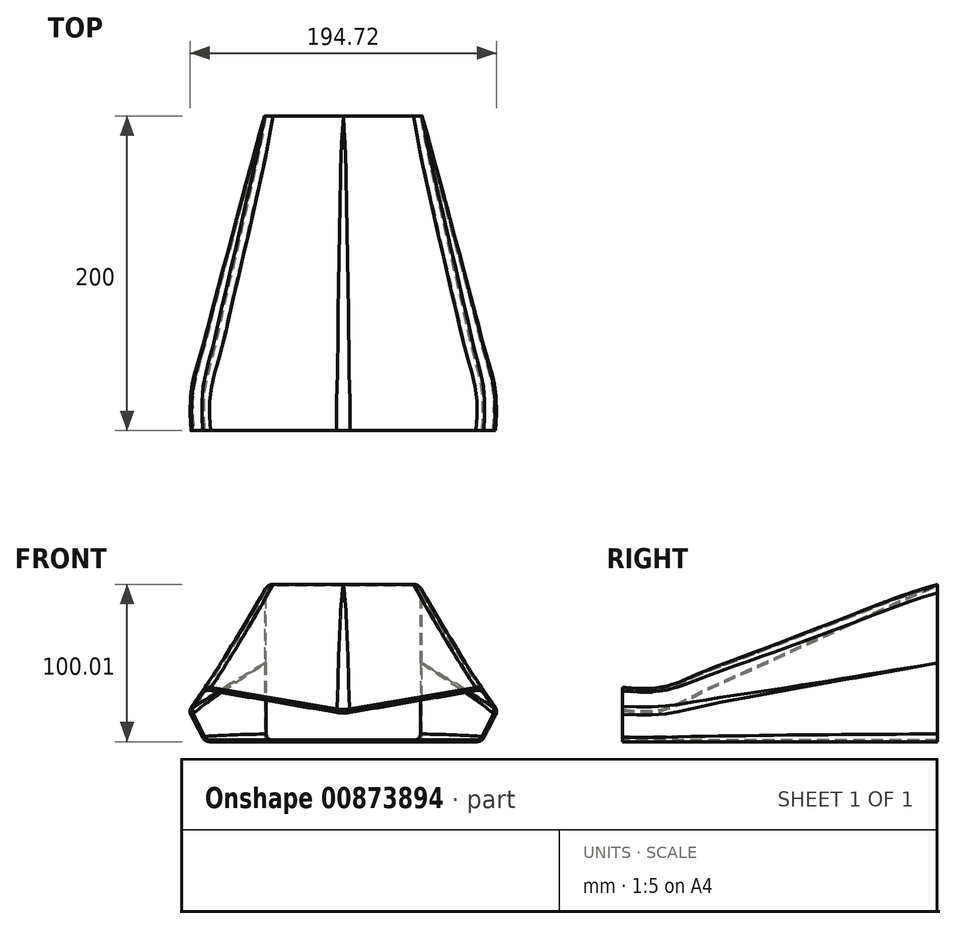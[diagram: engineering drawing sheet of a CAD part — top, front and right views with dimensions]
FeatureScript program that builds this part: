
annotation { "Feature Type Name" : "Feature", "Feature Type Description" : "" }
export const myFeature = defineFeature(function(context is Context, id is Id, definition is map)
    precondition{}
    {
        {
            var Q0;
            Q0=qCreatedBy(makeId("Front.planeOp"),FACE);
            var sketch = newSketch(context, id + "F0", { "sketchPlane" : qUnion([Q0])});
            skLineSegment(sketch, "E0.bottom", {"start": v(50, -50) * mm, "end": v(-50, -50) * mm});
            skLineSegment(sketch, "E0.top", {"start": v(50, 50) * mm, "end": v(-50, 50) * mm});
            skLineSegment(sketch, "E0.left", {"start": v(50, -50) * mm, "end": v(50, 50) * mm});
            skLineSegment(sketch, "E0.right", {"start": v(-50, -50) * mm, "end": v(-50, 50) * mm});
            skPoint(sketch, "E0.middle", {"position": v(0, 0) * mm});
            skPoint(sketch, "E1", {"position": v(-50, 0) * mm});
            skPoint(sketch, "E2", {"position": v(50, 0) * mm});
            skPoint(sketch, "E3", {"position": v(0, 50) * mm});
            skSolve(sketch);
        }
        {
            var Q0;
            Q0=qCreatedBy(makeId("Front.planeOp"),FACE);
            cPlane(context, id + "F1", {"entities" : qUnion([Q0]), "cplaneType" : CPlaneType.OFFSET, "offset" : 200 * mm, "width" : 150 * mm, "height" : 150 * mm});
        }
        {
            var Q0;
            Q0=qCreatedBy(id+"F1.planeOp",FACE);
            var sketch = newSketch(context, id + "F2", { "sketchPlane" : qUnion([Q0])});
            skLineSegment(sketch, "E4.0.0", {"start": v(50, -50) * mm, "end": v(50, 50) * mm, "construction": true});
            skLineSegment(sketch, "E4.0.1", {"start": v(50, 50) * mm, "end": v(-50, 50) * mm, "construction": true});
            skLineSegment(sketch, "E4.0.2", {"start": v(-50, 50) * mm, "end": v(-50, -50) * mm, "construction": true});
            skLineSegment(sketch, "E4.0.3", {"start": v(-50, -50) * mm, "end": v(50, -50) * mm, "construction": true});
            skLineSegment(sketch, "E5", {"start": v(-87.5, -50) * mm, "end": v(87.5, -50) * mm});
            skPoint(sketch, "E6", {"position": v(0, -50) * mm});
            skLineSegment(sketch, "E7", {"start": v(-87.5, -50) * mm, "end": v(-97.5, -30) * mm});
            skLineSegment(sketch, "E8", {"start": v(-97.5, -30) * mm, "end": v(-87.5, -15) * mm});
            skLineSegment(sketch, "E9", {"start": v(-87.5, -15) * mm, "end": v(0, -30) * mm});
            skLineSegment(sketch, "E10", {"start": v(0, -30) * mm, "end": v(87.5, -15) * mm});
            skLineSegment(sketch, "E11", {"start": v(87.5, -15) * mm, "end": v(97.5, -30) * mm});
            skLineSegment(sketch, "E12", {"start": v(97.5, -30) * mm, "end": v(87.5, -50) * mm});
            skLineSegment(sketch, "E13", {"start": v(-97.5, -30) * mm, "end": v(97.5, -30) * mm, "construction": true});
            skPoint(sketch, "E14", {"position": v(0, -30) * mm});
            skLineSegment(sketch, "E15", {"start": v(-87.5, -15) * mm, "end": v(87.5, -15) * mm, "construction": true});
            skPoint(sketch, "E16", {"position": v(0, -15) * mm});
            skSolve(sketch);
        }
        {
            var Q0;
            Q0=qCreatedBy(makeId("Front.planeOp"),FACE);
            cPlane(context, id + "F3", {"entities" : qUnion([Q0]), "cplaneType" : CPlaneType.OFFSET, "offset" : 175 * mm, "width" : 150 * mm, "height" : 150 * mm});
        }
        {
            var Q0;
            Q0=qCreatedBy(id+"F3.planeOp",FACE);
            var sketch = newSketch(context, id + "F4", { "sketchPlane" : qUnion([Q0])});
            skLineSegment(sketch, "E17.0.0", {"start": v(87.5, -50) * mm, "end": v(97.5, -30) * mm});
            skLineSegment(sketch, "E17.0.1", {"start": v(97.5, -30) * mm, "end": v(87.5, -15) * mm});
            skLineSegment(sketch, "E17.0.2", {"start": v(87.5, -15) * mm, "end": v(0, -30) * mm});
            skLineSegment(sketch, "E17.0.3", {"start": v(0, -30) * mm, "end": v(-87.5, -15) * mm});
            skLineSegment(sketch, "E17.0.4", {"start": v(-87.5, -15) * mm, "end": v(-97.5, -30) * mm});
            skLineSegment(sketch, "E17.0.5", {"start": v(-97.5, -30) * mm, "end": v(-87.5, -50) * mm});
            skLineSegment(sketch, "E17.0.6", {"start": v(-87.5, -50) * mm, "end": v(87.5, -50) * mm});
            skSolve(sketch);
        }
        {
            var Q0;
            Q0=qCreatedBy(makeId("Front.planeOp"),FACE);
            cPlane(context, id + "F5", {"entities" : qUnion([Q0]), "cplaneType" : CPlaneType.OFFSET, "offset" : 150 * mm, "width" : 150 * mm, "height" : 150 * mm});
        }
        {
            var Q0;
            Q0=qCreatedBy(id+"F5.planeOp",FACE);
            var sketch = newSketch(context, id + "F6", { "sketchPlane" : qUnion([Q0])});
            skPoint(sketch, "E18.0", {"position": v(-50, 50) * mm});
            skPoint(sketch, "E19.0", {"position": v(50, 50) * mm});
            skPoint(sketch, "E20.0", {"position": v(0, 50) * mm});
            skPoint(sketch, "E21.0", {"position": v(50, 0) * mm});
            skPoint(sketch, "E22.0", {"position": v(50, -50) * mm});
            skPoint(sketch, "E23.0", {"position": v(-50, 0) * mm});
            skPoint(sketch, "E24.0", {"position": v(-50, -50) * mm});
            skPoint(sketch, "E25.0", {"position": v(-87.5, -50) * mm});
            skPoint(sketch, "E26.0", {"position": v(-97.5, -30) * mm});
            skPoint(sketch, "E27.0", {"position": v(-87.5, -15) * mm});
            skPoint(sketch, "E28.0", {"position": v(87.5, -50) * mm});
            skPoint(sketch, "E29.0", {"position": v(97.5, -30) * mm});
            skPoint(sketch, "E30.0", {"position": v(87.5, -15) * mm});
            skLineSegment(sketch, "E31", {"start": v(-87.5, -15) * mm, "end": v(-50, 50) * mm, "construction": true});
            skLineSegment(sketch, "E32", {"start": v(-97.5, -30) * mm, "end": v(-50, 0) * mm, "construction": true});
            skLineSegment(sketch, "E33", {"start": v(-87.5, -50) * mm, "end": v(-50, -50) * mm, "construction": true});
            skPoint(sketch, "E34.0", {"position": v(0, -30) * mm});
            skLineSegment(sketch, "E35", {"start": v(0, -30) * mm, "end": v(0, 50) * mm, "construction": true});
            skLineSegment(sketch, "E36", {"start": v(87.5, -15) * mm, "end": v(50, 50) * mm, "construction": true});
            skLineSegment(sketch, "E37", {"start": v(97.5, -30) * mm, "end": v(50, 0) * mm, "construction": true});
            skLineSegment(sketch, "E38", {"start": v(87.5, -50) * mm, "end": v(50, -50) * mm, "construction": true});
            skPoint(sketch, "E39", {"position": v(-82, -50) * mm});
            skPoint(sketch, "E40", {"position": v(82, -50) * mm});
            skPoint(sketch, "E41", {"position": v(-90.74, -25.73) * mm});
            skPoint(sketch, "E42", {"position": v(90.74, -25.73) * mm});
            skPoint(sketch, "E43", {"position": v(-82, -5.47) * mm});
            skPoint(sketch, "E44", {"position": v(82, -5.47) * mm});
            skPoint(sketch, "E45", {"position": v(0, -18.5) * mm});
            skLineSegment(sketch, "E46", {"start": v(-82, -50) * mm, "end": v(82, -50) * mm});
            skLineSegment(sketch, "E47", {"start": v(82, -50) * mm, "end": v(90.74, -25.73) * mm});
            skLineSegment(sketch, "E48", {"start": v(90.74, -25.73) * mm, "end": v(82, -5.47) * mm});
            skLineSegment(sketch, "E49", {"start": v(82, -5.47) * mm, "end": v(0, -18.5) * mm});
            skLineSegment(sketch, "E50", {"start": v(0, -18.5) * mm, "end": v(-82, -5.47) * mm});
            skLineSegment(sketch, "E51", {"start": v(-82, -5.47) * mm, "end": v(-90.74, -25.73) * mm});
            skLineSegment(sketch, "E52", {"start": v(-90.74, -25.73) * mm, "end": v(-82, -50) * mm});
            skSolve(sketch);
        }
        {
            var Q0;
            Q0=qCreatedBy(makeId("Front.planeOp"),FACE);
            cPlane(context, id + "F7", {"entities" : qUnion([Q0]), "cplaneType" : CPlaneType.OFFSET, "offset" : 125 * mm, "width" : 150 * mm, "height" : 150 * mm});
        }
        {
            var Q0;
            Q0=qCreatedBy(id+"F7.planeOp",FACE);
            var sketch = newSketch(context, id + "F8", { "sketchPlane" : qUnion([Q0])});
            skPoint(sketch, "E53.0", {"position": v(-82, -50) * mm});
            skPoint(sketch, "E54.0", {"position": v(-90.74, -25.73) * mm});
            skPoint(sketch, "E55.0", {"position": v(-82, -5.47) * mm});
            skPoint(sketch, "E56.0", {"position": v(0, -18.5) * mm});
            skPoint(sketch, "E57.0", {"position": v(82, -5.47) * mm});
            skPoint(sketch, "E58.0", {"position": v(90.74, -25.73) * mm});
            skPoint(sketch, "E59.0", {"position": v(82, -50) * mm});
            skLineSegment(sketch, "E60.0", {"start": v(-87.5, -50) * mm, "end": v(-50, -50) * mm, "construction": true});
            skLineSegment(sketch, "E61.0", {"start": v(-97.5, -30) * mm, "end": v(-50, 0) * mm, "construction": true});
            skLineSegment(sketch, "E62.0", {"start": v(-87.5, -15) * mm, "end": v(-50, 50) * mm, "construction": true});
            skLineSegment(sketch, "E63.0", {"start": v(0, -30) * mm, "end": v(0, 50) * mm, "construction": true});
            skLineSegment(sketch, "E64.0", {"start": v(87.5, -15) * mm, "end": v(50, 50) * mm, "construction": true});
            skLineSegment(sketch, "E65.0", {"start": v(97.5, -30) * mm, "end": v(50, 0) * mm, "construction": true});
            skLineSegment(sketch, "E66.0", {"start": v(87.5, -50) * mm, "end": v(50, -50) * mm, "construction": true});
            skPoint(sketch, "E67", {"position": v(-76.5, -50) * mm});
            skPoint(sketch, "E68", {"position": v(-83.97, -21.46) * mm});
            skPoint(sketch, "E69", {"position": v(-76.5, 4.06) * mm});
            skPoint(sketch, "E70", {"position": v(76.5, 4.06) * mm});
            skPoint(sketch, "E71", {"position": v(83.97, -21.46) * mm});
            skPoint(sketch, "E72", {"position": v(76.5, -50) * mm});
            skPoint(sketch, "E73", {"position": v(0, -7) * mm});
            skLineSegment(sketch, "E74", {"start": v(-76.5, -50) * mm, "end": v(76.5, -50) * mm});
            skLineSegment(sketch, "E75", {"start": v(76.5, -50) * mm, "end": v(83.97, -21.46) * mm});
            skLineSegment(sketch, "E76", {"start": v(83.97, -21.46) * mm, "end": v(76.5, 4.06) * mm});
            skLineSegment(sketch, "E77", {"start": v(76.5, 4.06) * mm, "end": v(0, -7) * mm});
            skLineSegment(sketch, "E78", {"start": v(0, -7) * mm, "end": v(-76.5, 4.06) * mm});
            skLineSegment(sketch, "E79", {"start": v(-76.5, 4.06) * mm, "end": v(-83.97, -21.46) * mm});
            skLineSegment(sketch, "E80", {"start": v(-83.97, -21.46) * mm, "end": v(-76.5, -50) * mm});
            skSolve(sketch);
        }
        {
            var Q0;
            Q0=qCreatedBy(makeId("Front.planeOp"),FACE);
            cPlane(context, id + "F9", {"entities" : qUnion([Q0]), "cplaneType" : CPlaneType.OFFSET, "offset" : 100 * mm, "width" : 150 * mm, "height" : 150 * mm});
        }
        {
            var Q0;
            Q0=qCreatedBy(id+"F9.planeOp",FACE);
            var sketch = newSketch(context, id + "F10", { "sketchPlane" : qUnion([Q0])});
            skPoint(sketch, "E81.0", {"position": v(-76.5, -50) * mm});
            skPoint(sketch, "E82.0", {"position": v(-83.97, -21.46) * mm});
            skPoint(sketch, "E83.0", {"position": v(-76.5, 4.06) * mm});
            skPoint(sketch, "E84.0", {"position": v(0, -7) * mm});
            skPoint(sketch, "E85.0", {"position": v(76.5, 4.06) * mm});
            skPoint(sketch, "E86.0", {"position": v(83.97, -21.46) * mm});
            skPoint(sketch, "E87.0", {"position": v(76.5, -50) * mm});
            skLineSegment(sketch, "E88.0", {"start": v(-87.5, -50) * mm, "end": v(-50, -50) * mm, "construction": true});
            skLineSegment(sketch, "E89.0", {"start": v(-97.5, -30) * mm, "end": v(-50, 0) * mm, "construction": true});
            skLineSegment(sketch, "E90.0", {"start": v(-87.5, -15) * mm, "end": v(-50, 50) * mm, "construction": true});
            skLineSegment(sketch, "E91.0", {"start": v(0, -30) * mm, "end": v(0, 50) * mm, "construction": true});
            skLineSegment(sketch, "E92.0", {"start": v(87.5, -15) * mm, "end": v(50, 50) * mm, "construction": true});
            skLineSegment(sketch, "E93.0", {"start": v(97.5, -30) * mm, "end": v(50, 0) * mm, "construction": true});
            skLineSegment(sketch, "E94.0", {"start": v(87.5, -50) * mm, "end": v(50, -50) * mm, "construction": true});
            skPoint(sketch, "E95", {"position": v(-71, -50) * mm});
            skPoint(sketch, "E96", {"position": v(71, -50) * mm});
            skPoint(sketch, "E97", {"position": v(77.2, -17.18) * mm});
            skPoint(sketch, "E98", {"position": v(-77.2, -17.18) * mm});
            skPoint(sketch, "E99", {"position": v(-71, 13.58) * mm});
            skPoint(sketch, "E100", {"position": v(71, 13.58) * mm});
            skPoint(sketch, "E101", {"position": v(0, 4.5) * mm});
            skLineSegment(sketch, "E102", {"start": v(71, -50) * mm, "end": v(-71, -50) * mm});
            skLineSegment(sketch, "E103", {"start": v(-71, -50) * mm, "end": v(-77.2, -17.18) * mm});
            skLineSegment(sketch, "E104", {"start": v(-77.2, -17.18) * mm, "end": v(-71, 13.58) * mm});
            skLineSegment(sketch, "E105", {"start": v(-71, 13.58) * mm, "end": v(0, 4.5) * mm});
            skLineSegment(sketch, "E106", {"start": v(0, 4.5) * mm, "end": v(71, 13.58) * mm});
            skLineSegment(sketch, "E107", {"start": v(71, 13.58) * mm, "end": v(77.2, -17.18) * mm});
            skLineSegment(sketch, "E108", {"start": v(77.2, -17.18) * mm, "end": v(71, -50) * mm});
            skSolve(sketch);
        }
        {
            var Q0;
            Q0=qCreatedBy(makeId("Front.planeOp"),FACE);
            cPlane(context, id + "F11", {"entities" : qUnion([Q0]), "cplaneType" : CPlaneType.OFFSET, "offset" : 75 * mm, "width" : 150 * mm, "height" : 150 * mm});
        }
        {
            var Q0;
            Q0=qCreatedBy(id+"F11.planeOp",FACE);
            var sketch = newSketch(context, id + "F12", { "sketchPlane" : qUnion([Q0])});
            skPoint(sketch, "E109.0", {"position": v(-71, -50) * mm});
            skPoint(sketch, "E110.0", {"position": v(-77.2, -17.18) * mm});
            skPoint(sketch, "E111.0", {"position": v(-71, 13.58) * mm});
            skPoint(sketch, "E112.0", {"position": v(0, 4.5) * mm});
            skPoint(sketch, "E113.0", {"position": v(71, 13.58) * mm});
            skPoint(sketch, "E114.0", {"position": v(77.2, -17.18) * mm});
            skPoint(sketch, "E115.0", {"position": v(71, -50) * mm});
            skLineSegment(sketch, "E116.0", {"start": v(-87.5, -50) * mm, "end": v(-50, -50) * mm, "construction": true});
            skLineSegment(sketch, "E117.0", {"start": v(-97.5, -30) * mm, "end": v(-50, 0) * mm, "construction": true});
            skLineSegment(sketch, "E118.0", {"start": v(-87.5, -15) * mm, "end": v(-50, 50) * mm, "construction": true});
            skLineSegment(sketch, "E119.0", {"start": v(0, -30) * mm, "end": v(0, 50) * mm, "construction": true});
            skLineSegment(sketch, "E120.0", {"start": v(87.5, -15) * mm, "end": v(50, 50) * mm, "construction": true});
            skLineSegment(sketch, "E121.0", {"start": v(97.5, -30) * mm, "end": v(50, 0) * mm, "construction": true});
            skLineSegment(sketch, "E122.0", {"start": v(87.5, -50) * mm, "end": v(50, -50) * mm, "construction": true});
            skPoint(sketch, "E123", {"position": v(-65.5, -50) * mm});
            skPoint(sketch, "E124", {"position": v(65.5, -50) * mm});
            skPoint(sketch, "E125", {"position": v(70.44, -12.91) * mm});
            skPoint(sketch, "E126", {"position": v(-70.44, -12.91) * mm});
            skPoint(sketch, "E127", {"position": v(-65.51, 23.11) * mm});
            skPoint(sketch, "E128", {"position": v(65.51, 23.11) * mm});
            skPoint(sketch, "E129", {"position": v(0, 16) * mm});
            skLineSegment(sketch, "E130", {"start": v(-65.5, -50) * mm, "end": v(65.5, -50) * mm});
            skLineSegment(sketch, "E131", {"start": v(65.5, -50) * mm, "end": v(70.44, -12.91) * mm});
            skLineSegment(sketch, "E132", {"start": v(70.44, -12.91) * mm, "end": v(65.51, 23.11) * mm});
            skLineSegment(sketch, "E133", {"start": v(65.51, 23.11) * mm, "end": v(0, 16) * mm});
            skLineSegment(sketch, "E134", {"start": v(0, 16) * mm, "end": v(-65.51, 23.11) * mm});
            skLineSegment(sketch, "E135", {"start": v(-65.51, 23.11) * mm, "end": v(-70.44, -12.91) * mm});
            skLineSegment(sketch, "E136", {"start": v(-70.44, -12.91) * mm, "end": v(-65.5, -50) * mm});
            skSolve(sketch);
        }
        {
            var Q0;
            Q0=qCreatedBy(makeId("Front.planeOp"),FACE);
            cPlane(context, id + "F13", {"entities" : qUnion([Q0]), "cplaneType" : CPlaneType.OFFSET, "offset" : 50 * mm, "width" : 150 * mm, "height" : 150 * mm});
        }
        {
            var Q0;
            Q0=qCreatedBy(id+"F13.planeOp",FACE);
            var sketch = newSketch(context, id + "F14", { "sketchPlane" : qUnion([Q0])});
            skPoint(sketch, "E137.0", {"position": v(-65.5, -50) * mm});
            skPoint(sketch, "E138.0", {"position": v(-70.44, -12.91) * mm});
            skPoint(sketch, "E139.0", {"position": v(-65.51, 23.11) * mm});
            skPoint(sketch, "E140.0", {"position": v(0, 16) * mm});
            skPoint(sketch, "E141.0", {"position": v(65.51, 23.11) * mm});
            skPoint(sketch, "E142.0", {"position": v(70.44, -12.91) * mm});
            skPoint(sketch, "E143.0", {"position": v(65.5, -50) * mm});
            skLineSegment(sketch, "E144.0", {"start": v(-87.5, -50) * mm, "end": v(-50, -50) * mm, "construction": true});
            skLineSegment(sketch, "E145.0", {"start": v(-97.5, -30) * mm, "end": v(-50, 0) * mm, "construction": true});
            skLineSegment(sketch, "E146.0", {"start": v(-87.5, -15) * mm, "end": v(-50, 50) * mm, "construction": true});
            skLineSegment(sketch, "E147.0", {"start": v(87.5, -15) * mm, "end": v(50, 50) * mm, "construction": true});
            skLineSegment(sketch, "E148.0", {"start": v(97.5, -30) * mm, "end": v(50, 0) * mm, "construction": true});
            skLineSegment(sketch, "E149.0", {"start": v(87.5, -50) * mm, "end": v(50, -50) * mm, "construction": true});
            skLineSegment(sketch, "E150.0", {"start": v(0, -30) * mm, "end": v(0, 50) * mm, "construction": true});
            skPoint(sketch, "E151", {"position": v(-60, -50) * mm});
            skPoint(sketch, "E152", {"position": v(60, -50) * mm});
            skPoint(sketch, "E153", {"position": v(63.68, -8.64) * mm});
            skPoint(sketch, "E154", {"position": v(-63.68, -8.64) * mm});
            skPoint(sketch, "E155", {"position": v(-60.02, 32.64) * mm});
            skPoint(sketch, "E156", {"position": v(60.02, 32.64) * mm});
            skPoint(sketch, "E157", {"position": v(0, 27.5) * mm});
            skLineSegment(sketch, "E158", {"start": v(-60, -50) * mm, "end": v(60, -50) * mm});
            skLineSegment(sketch, "E159", {"start": v(60, -50) * mm, "end": v(63.68, -8.64) * mm});
            skLineSegment(sketch, "E160", {"start": v(63.68, -8.64) * mm, "end": v(60.02, 32.64) * mm});
            skLineSegment(sketch, "E161", {"start": v(60.02, 32.64) * mm, "end": v(0, 27.5) * mm});
            skLineSegment(sketch, "E162", {"start": v(0, 27.5) * mm, "end": v(-60.02, 32.64) * mm});
            skLineSegment(sketch, "E163", {"start": v(-60.02, 32.64) * mm, "end": v(-63.68, -8.64) * mm});
            skLineSegment(sketch, "E164", {"start": v(-63.68, -8.64) * mm, "end": v(-60, -50) * mm});
            skSolve(sketch);
        }
        {
            var Q0;
            Q0=qCreatedBy(makeId("Front.planeOp"),FACE);
            cPlane(context, id + "F15", {"entities" : qUnion([Q0]), "cplaneType" : CPlaneType.OFFSET, "offset" : 25 * mm, "width" : 150 * mm, "height" : 150 * mm});
        }
        {
            var Q0;
            Q0=qCreatedBy(id+"F15.planeOp",FACE);
            var sketch = newSketch(context, id + "F16", { "sketchPlane" : qUnion([Q0])});
            skPoint(sketch, "E165.0", {"position": v(-60, -50) * mm});
            skPoint(sketch, "E166.0", {"position": v(-63.68, -8.64) * mm});
            skPoint(sketch, "E167.0", {"position": v(-60.02, 32.64) * mm});
            skPoint(sketch, "E168.0", {"position": v(0, 27.5) * mm});
            skPoint(sketch, "E169.0", {"position": v(60.02, 32.64) * mm});
            skPoint(sketch, "E170.0", {"position": v(63.68, -8.64) * mm});
            skPoint(sketch, "E171.0", {"position": v(60, -50) * mm});
            skLineSegment(sketch, "E172.0", {"start": v(-87.5, -50) * mm, "end": v(-50, -50) * mm, "construction": true});
            skLineSegment(sketch, "E173.0", {"start": v(-97.5, -30) * mm, "end": v(-50, 0) * mm, "construction": true});
            skLineSegment(sketch, "E174.0", {"start": v(-87.5, -15) * mm, "end": v(-50, 50) * mm, "construction": true});
            skLineSegment(sketch, "E175.0", {"start": v(0, -30) * mm, "end": v(0, 50) * mm, "construction": true});
            skLineSegment(sketch, "E176.0", {"start": v(87.5, -15) * mm, "end": v(50, 50) * mm, "construction": true});
            skLineSegment(sketch, "E177.0", {"start": v(97.5, -30) * mm, "end": v(50, 0) * mm, "construction": true});
            skLineSegment(sketch, "E178.0", {"start": v(87.5, -50) * mm, "end": v(50, -50) * mm, "construction": true});
            skPoint(sketch, "E179", {"position": v(-54.5, -50) * mm});
            skPoint(sketch, "E180", {"position": v(-56.92, -4.37) * mm});
            skPoint(sketch, "E181", {"position": v(-54.52, 42.17) * mm});
            skPoint(sketch, "E182", {"position": v(54.52, 42.17) * mm});
            skPoint(sketch, "E183", {"position": v(0, 39) * mm});
            skPoint(sketch, "E184", {"position": v(56.92, -4.37) * mm});
            skPoint(sketch, "E185", {"position": v(54.5, -50) * mm});
            skLineSegment(sketch, "E186", {"start": v(-54.5, -50) * mm, "end": v(54.5, -50) * mm});
            skLineSegment(sketch, "E187", {"start": v(54.5, -50) * mm, "end": v(56.92, -4.37) * mm});
            skLineSegment(sketch, "E188", {"start": v(56.92, -4.37) * mm, "end": v(54.52, 42.17) * mm});
            skLineSegment(sketch, "E189", {"start": v(54.52, 42.17) * mm, "end": v(0, 39) * mm});
            skLineSegment(sketch, "E190", {"start": v(0, 39) * mm, "end": v(-54.52, 42.17) * mm});
            skLineSegment(sketch, "E191", {"start": v(-54.52, 42.17) * mm, "end": v(-56.92, -4.37) * mm});
            skLineSegment(sketch, "E192", {"start": v(-56.92, -4.37) * mm, "end": v(-54.5, -50) * mm});
            skSolve(sketch);
        }
        {
            var Q0;
            Q0=qCreatedBy(makeId("Front.planeOp"),FACE);
            var sketch = newSketch(context, id + "F17", { "sketchPlane" : qUnion([Q0])});
            skPoint(sketch, "E193.0", {"position": v(-50, -50) * mm});
            skPoint(sketch, "E194.0", {"position": v(-50, 0) * mm});
            skPoint(sketch, "E195.0", {"position": v(-50, 50) * mm});
            skPoint(sketch, "E196.0", {"position": v(0, 50) * mm});
            skPoint(sketch, "E197.0", {"position": v(50, 50) * mm});
            skPoint(sketch, "E198.0", {"position": v(50, 0) * mm});
            skPoint(sketch, "E199.0", {"position": v(50, -50) * mm});
            skLineSegment(sketch, "E200", {"start": v(-50, -50) * mm, "end": v(50, -50) * mm});
            skLineSegment(sketch, "E201", {"start": v(50, -50) * mm, "end": v(50, 0) * mm});
            skLineSegment(sketch, "E202", {"start": v(50, 0) * mm, "end": v(50, 50) * mm});
            skLineSegment(sketch, "E203", {"start": v(50, 50) * mm, "end": v(0, 50) * mm});
            skLineSegment(sketch, "E204", {"start": v(0, 50) * mm, "end": v(-50, 50) * mm});
            skLineSegment(sketch, "E205", {"start": v(-50, 50) * mm, "end": v(-50, 0) * mm});
            skLineSegment(sketch, "E206", {"start": v(-50, 0) * mm, "end": v(-50, -50) * mm});
            skSolve(sketch);
        }
        {
            var Q0;
            Q0=makeQuery(id+"F17.imprint","IMPRINT",FACE,{"disambiguationData":[TD([[makeQuery(id+"F17.imprint","IMPRINT",EDGE,{"derivedFrom":sQuery(id+"F17.wireOp",EDGE,"E200")}),1.0]])]});
            var Q1;
            Q1=makeQuery(id+"F16.imprint","IMPRINT",FACE,{"disambiguationData":[TD([[makeQuery(id+"F16.imprint","IMPRINT",EDGE,{"derivedFrom":sQuery(id+"F16.wireOp",EDGE,"E186")}),1.0]])]});
            var Q2;
            Q2=makeQuery(id+"F14.imprint","IMPRINT",FACE,{"disambiguationData":[TD([[makeQuery(id+"F14.imprint","IMPRINT",EDGE,{"derivedFrom":sQuery(id+"F14.wireOp",EDGE,"E158")}),1.0]])]});
            var Q3;
            Q3=makeQuery(id+"F12.imprint","IMPRINT",FACE,{"disambiguationData":[TD([[makeQuery(id+"F12.imprint","IMPRINT",EDGE,{"derivedFrom":sQuery(id+"F12.wireOp",EDGE,"E130")}),1.0]])]});
            var Q4;
            Q4=makeQuery(id+"F10.imprint","IMPRINT",FACE,{"disambiguationData":[TD([[makeQuery(id+"F10.imprint","IMPRINT",EDGE,{"derivedFrom":sQuery(id+"F10.wireOp",EDGE,"E102")}),-1.0]])]});
            var Q5;
            Q5=makeQuery(id+"F8.imprint","IMPRINT",FACE,{"disambiguationData":[TD([[makeQuery(id+"F8.imprint","IMPRINT",EDGE,{"derivedFrom":sQuery(id+"F8.wireOp",EDGE,"E74")}),1.0]])]});
            var Q6;
            Q6=makeQuery(id+"F6.imprint","IMPRINT",FACE,{"disambiguationData":[TD([[makeQuery(id+"F6.imprint","IMPRINT",EDGE,{"derivedFrom":sQuery(id+"F6.wireOp",EDGE,"E46")}),1.0]])]});
            var Q7;
            Q7=makeQuery(id+"F4.imprint","IMPRINT",FACE,{"disambiguationData":[TD([[makeQuery(id+"F4.imprint","IMPRINT",EDGE,{"derivedFrom":sQuery(id+"F4.wireOp",EDGE,"E17.0.0")}),1.0]])]});
            var Q8;
            Q8=makeQuery(id+"F2.imprint","IMPRINT",FACE,{"disambiguationData":[TD([[makeQuery(id+"F2.imprint","IMPRINT",EDGE,{"derivedFrom":sQuery(id+"F2.wireOp",EDGE,"E5")}),1.0]])]});
            loft(context, id + "F18", {"sheetProfilesArray" : [{ "sheetProfileEntities" : qUnion([Q0]) }, { "sheetProfileEntities" : qUnion([Q1]) }, { "sheetProfileEntities" : qUnion([Q2]) }, { "sheetProfileEntities" : qUnion([Q3]) }, { "sheetProfileEntities" : qUnion([Q4]) }, { "sheetProfileEntities" : qUnion([Q5]) }, { "sheetProfileEntities" : qUnion([Q6]) }, { "sheetProfileEntities" : qUnion([Q7]) }, { "sheetProfileEntities" : qUnion([Q8]) }]});
        }
        {
            var Q0;
            Q0=makeQuery(id+"F18.opLoft","SWEPT_EDGE",EDGE,{"disambiguationData":[OSD([sQuery(id+"F2.wireOp",EDGE,"E10"),sQuery(id+"F2.wireOp",EDGE,"E11"),sQuery(id+"F4.wireOp",EDGE,"E17.0.1"),sQuery(id+"F4.wireOp",EDGE,"E17.0.2"),sQuery(id+"F6.wireOp",EDGE,"E48"),sQuery(id+"F6.wireOp",EDGE,"E49"),sQuery(id+"F8.wireOp",EDGE,"E76"),sQuery(id+"F8.wireOp",EDGE,"E77"),sQuery(id+"F10.wireOp",EDGE,"E106"),sQuery(id+"F10.wireOp",EDGE,"E107"),sQuery(id+"F12.wireOp",EDGE,"E132"),sQuery(id+"F12.wireOp",EDGE,"E133"),sQuery(id+"F14.wireOp",EDGE,"E160"),sQuery(id+"F14.wireOp",EDGE,"E161"),sQuery(id+"F16.wireOp",EDGE,"E188"),sQuery(id+"F16.wireOp",EDGE,"E189"),sQuery(id+"F17.wireOp",EDGE,"E202"),sQuery(id+"F17.wireOp",EDGE,"E203")])]});
            var Q1;
            Q1=makeQuery(id+"F18.opLoft","SWEPT_EDGE",EDGE,{"disambiguationData":[OSD([sQuery(id+"F2.wireOp",EDGE,"E8"),sQuery(id+"F2.wireOp",EDGE,"E9"),sQuery(id+"F4.wireOp",EDGE,"E17.0.3"),sQuery(id+"F4.wireOp",EDGE,"E17.0.4"),sQuery(id+"F6.wireOp",EDGE,"E50"),sQuery(id+"F6.wireOp",EDGE,"E51"),sQuery(id+"F8.wireOp",EDGE,"E78"),sQuery(id+"F8.wireOp",EDGE,"E79"),sQuery(id+"F10.wireOp",EDGE,"E104"),sQuery(id+"F10.wireOp",EDGE,"E105"),sQuery(id+"F12.wireOp",EDGE,"E134"),sQuery(id+"F12.wireOp",EDGE,"E135"),sQuery(id+"F14.wireOp",EDGE,"E162"),sQuery(id+"F14.wireOp",EDGE,"E163"),sQuery(id+"F16.wireOp",EDGE,"E190"),sQuery(id+"F16.wireOp",EDGE,"E191"),sQuery(id+"F17.wireOp",EDGE,"E204"),sQuery(id+"F17.wireOp",EDGE,"E205")])]});
            var Q2;
            Q2=makeQuery(id+"F18.opLoft","SWEPT_EDGE",EDGE,{"disambiguationData":[OSD([sQuery(id+"F2.wireOp",EDGE,"E7"),sQuery(id+"F2.wireOp",EDGE,"E8"),sQuery(id+"F4.wireOp",EDGE,"E17.0.4"),sQuery(id+"F4.wireOp",EDGE,"E17.0.5"),sQuery(id+"F6.wireOp",EDGE,"E51"),sQuery(id+"F6.wireOp",EDGE,"E52"),sQuery(id+"F8.wireOp",EDGE,"E79"),sQuery(id+"F8.wireOp",EDGE,"E80"),sQuery(id+"F10.wireOp",EDGE,"E103"),sQuery(id+"F10.wireOp",EDGE,"E104"),sQuery(id+"F12.wireOp",EDGE,"E135"),sQuery(id+"F12.wireOp",EDGE,"E136"),sQuery(id+"F14.wireOp",EDGE,"E163"),sQuery(id+"F14.wireOp",EDGE,"E164"),sQuery(id+"F16.wireOp",EDGE,"E191"),sQuery(id+"F16.wireOp",EDGE,"E192"),sQuery(id+"F17.wireOp",EDGE,"E205"),sQuery(id+"F17.wireOp",EDGE,"E206")])]});
            var Q3;
            Q3=makeQuery(id+"F18.opLoft","SWEPT_EDGE",EDGE,{"disambiguationData":[OSD([sQuery(id+"F2.wireOp",EDGE,"E11"),sQuery(id+"F2.wireOp",EDGE,"E12"),sQuery(id+"F4.wireOp",EDGE,"E17.0.0"),sQuery(id+"F4.wireOp",EDGE,"E17.0.1"),sQuery(id+"F6.wireOp",EDGE,"E47"),sQuery(id+"F6.wireOp",EDGE,"E48"),sQuery(id+"F8.wireOp",EDGE,"E75"),sQuery(id+"F8.wireOp",EDGE,"E76"),sQuery(id+"F10.wireOp",EDGE,"E107"),sQuery(id+"F10.wireOp",EDGE,"E108"),sQuery(id+"F12.wireOp",EDGE,"E131"),sQuery(id+"F12.wireOp",EDGE,"E132"),sQuery(id+"F14.wireOp",EDGE,"E159"),sQuery(id+"F14.wireOp",EDGE,"E160"),sQuery(id+"F16.wireOp",EDGE,"E187"),sQuery(id+"F16.wireOp",EDGE,"E188"),sQuery(id+"F17.wireOp",EDGE,"E201"),sQuery(id+"F17.wireOp",EDGE,"E202")])]});
            var Q4;
            Q4=makeQuery(id+"F18.opLoft","SWEPT_EDGE",EDGE,{"disambiguationData":[OSD([sQuery(id+"F2.wireOp",EDGE,"E5"),sQuery(id+"F2.wireOp",EDGE,"E12"),sQuery(id+"F4.wireOp",EDGE,"E17.0.0"),sQuery(id+"F4.wireOp",EDGE,"E17.0.6"),sQuery(id+"F6.wireOp",EDGE,"E46"),sQuery(id+"F6.wireOp",EDGE,"E47"),sQuery(id+"F8.wireOp",EDGE,"E74"),sQuery(id+"F8.wireOp",EDGE,"E75"),sQuery(id+"F10.wireOp",EDGE,"E102"),sQuery(id+"F10.wireOp",EDGE,"E108"),sQuery(id+"F12.wireOp",EDGE,"E130"),sQuery(id+"F12.wireOp",EDGE,"E131"),sQuery(id+"F14.wireOp",EDGE,"E158"),sQuery(id+"F14.wireOp",EDGE,"E159"),sQuery(id+"F16.wireOp",EDGE,"E186"),sQuery(id+"F16.wireOp",EDGE,"E187"),sQuery(id+"F17.wireOp",EDGE,"E200"),sQuery(id+"F17.wireOp",EDGE,"E201")])]});
            var Q5;
            Q5=makeQuery(id+"F18.opLoft","SWEPT_EDGE",EDGE,{"disambiguationData":[OSD([sQuery(id+"F2.wireOp",EDGE,"E5"),sQuery(id+"F2.wireOp",EDGE,"E7"),sQuery(id+"F4.wireOp",EDGE,"E17.0.5"),sQuery(id+"F4.wireOp",EDGE,"E17.0.6"),sQuery(id+"F6.wireOp",EDGE,"E46"),sQuery(id+"F6.wireOp",EDGE,"E52"),sQuery(id+"F8.wireOp",EDGE,"E74"),sQuery(id+"F8.wireOp",EDGE,"E80"),sQuery(id+"F10.wireOp",EDGE,"E102"),sQuery(id+"F10.wireOp",EDGE,"E103"),sQuery(id+"F12.wireOp",EDGE,"E130"),sQuery(id+"F12.wireOp",EDGE,"E136"),sQuery(id+"F14.wireOp",EDGE,"E158"),sQuery(id+"F14.wireOp",EDGE,"E164"),sQuery(id+"F16.wireOp",EDGE,"E186"),sQuery(id+"F16.wireOp",EDGE,"E192"),sQuery(id+"F17.wireOp",EDGE,"E200"),sQuery(id+"F17.wireOp",EDGE,"E206")])]});
            fillet(context, id + "F19", {"entities" : qUnion([Q0, Q1, Q2, Q3, Q4, Q5]), "radius" : 5 * mm, "tangentPropagation" : true, "allowEdgeOverflow" : false});
        }
        {
            var Q0;
            Q0=makeQuery(id+"F18.opLoft","SWEPT_EDGE",EDGE,{"disambiguationData":[OSD([sQuery(id+"F2.wireOp",EDGE,"E9"),sQuery(id+"F2.wireOp",EDGE,"E10"),sQuery(id+"F4.wireOp",EDGE,"E17.0.2"),sQuery(id+"F4.wireOp",EDGE,"E17.0.3"),sQuery(id+"F6.wireOp",EDGE,"E49"),sQuery(id+"F6.wireOp",EDGE,"E50"),sQuery(id+"F8.wireOp",EDGE,"E77"),sQuery(id+"F8.wireOp",EDGE,"E78"),sQuery(id+"F10.wireOp",EDGE,"E105"),sQuery(id+"F10.wireOp",EDGE,"E106"),sQuery(id+"F12.wireOp",EDGE,"E133"),sQuery(id+"F12.wireOp",EDGE,"E134"),sQuery(id+"F14.wireOp",EDGE,"E161"),sQuery(id+"F14.wireOp",EDGE,"E162"),sQuery(id+"F16.wireOp",EDGE,"E189"),sQuery(id+"F16.wireOp",EDGE,"E190"),sQuery(id+"F17.wireOp",EDGE,"E203"),sQuery(id+"F17.wireOp",EDGE,"E204")])]});
            fillet(context, id + "F20", {"entities" : qUnion([Q0]), "radius" : 25 * mm, "tangentPropagation" : true, "allowEdgeOverflow" : false});
        }
        {
            var Q0;
            Q0=makeQuery(id+"F18.opLoft","CAP_FACE",FACE,{"disambiguationData":[OSD([makeQuery(id+"F2.imprint","IMPRINT",FACE,{"disambiguationData":[TD([[makeQuery(id+"F2.imprint","IMPRINT",EDGE,{"derivedFrom":sQuery(id+"F2.wireOp",EDGE,"E5")}),1.0]])]})])],"isStart":true});
            var Q1;
            Q1=makeQuery(id+"F18.opLoft","CAP_FACE",FACE,{"disambiguationData":[OSD([makeQuery(id+"F17.imprint","IMPRINT",FACE,{"disambiguationData":[TD([[makeQuery(id+"F17.imprint","IMPRINT",EDGE,{"derivedFrom":sQuery(id+"F17.wireOp",EDGE,"E200")}),1.0]])]})])],"isStart":true});
            shell(context, id + "F21", {"entities" : qUnion([Q0, Q1]), "thickness" : 1 * mm});
        }
    });
